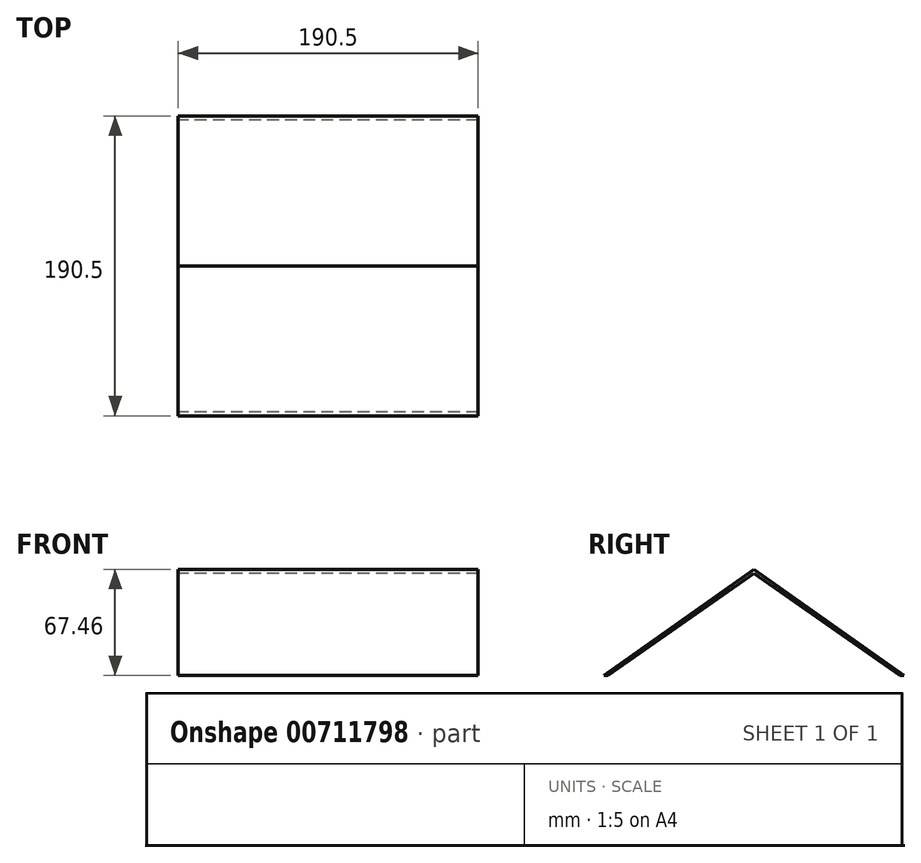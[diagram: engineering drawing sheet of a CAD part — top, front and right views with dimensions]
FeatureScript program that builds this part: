
annotation { "Feature Type Name" : "Feature", "Feature Type Description" : "" }
export const myFeature = defineFeature(function(context is Context, id is Id, definition is map)
    precondition{}
    {
        {
            var Q0;
            Q0=qCreatedBy(makeId("Right.planeOp"),FACE);
            var sketch = newSketch(context, id + "F0", { "sketchPlane" : qUnion([Q0])});
            skLineSegment(sketch, "E0", {"start": v(-95.25, 0) * mm, "end": v(0, 67.46) * mm});
            skLineSegment(sketch, "E1", {"start": v(0, 67.46) * mm, "end": v(0, 64.92) * mm});
            skLineSegment(sketch, "E2", {"start": v(0, 64.92) * mm, "end": v(-92.71, 0) * mm});
            skLineSegment(sketch, "E3", {"start": v(-92.7, 0) * mm, "end": v(-95.25, 0) * mm});
            skLineSegment(sketch, "E4", {"start": v(0, -2.55) * mm, "end": v(0, 27.37) * mm, "construction": true});
            skLineSegment(sketch, "E5", {"start": v(0, 67.46) * mm, "end": v(-35.44, 67.46) * mm, "construction": true});
            skLineSegment(sketch, "E6", {"start": v(-92.71, 0) * mm, "end": v(3.87, 0) * mm, "construction": true});
            skLineSegment(sketch, "E7.MirrorCS", {"start": v(95.25, 0) * mm, "end": v(0, 67.46) * mm});
            skLineSegment(sketch, "E8.MirrorCS", {"start": v(0, 64.92) * mm, "end": v(92.71, 0) * mm});
            skLineSegment(sketch, "E9.MirrorCS", {"start": v(92.7, 0) * mm, "end": v(95.25, 0) * mm});
            skSolve(sketch);
        }
        {
            var Q0;
            Q0 = qSketchRegion(id + "F0", true);
            extrude(context, id + "F1", {"entities" : qUnion([Q0]), "depth" : 190.5 * mm, "offsetDistance" : 25.4 * mm});
        }
    });
